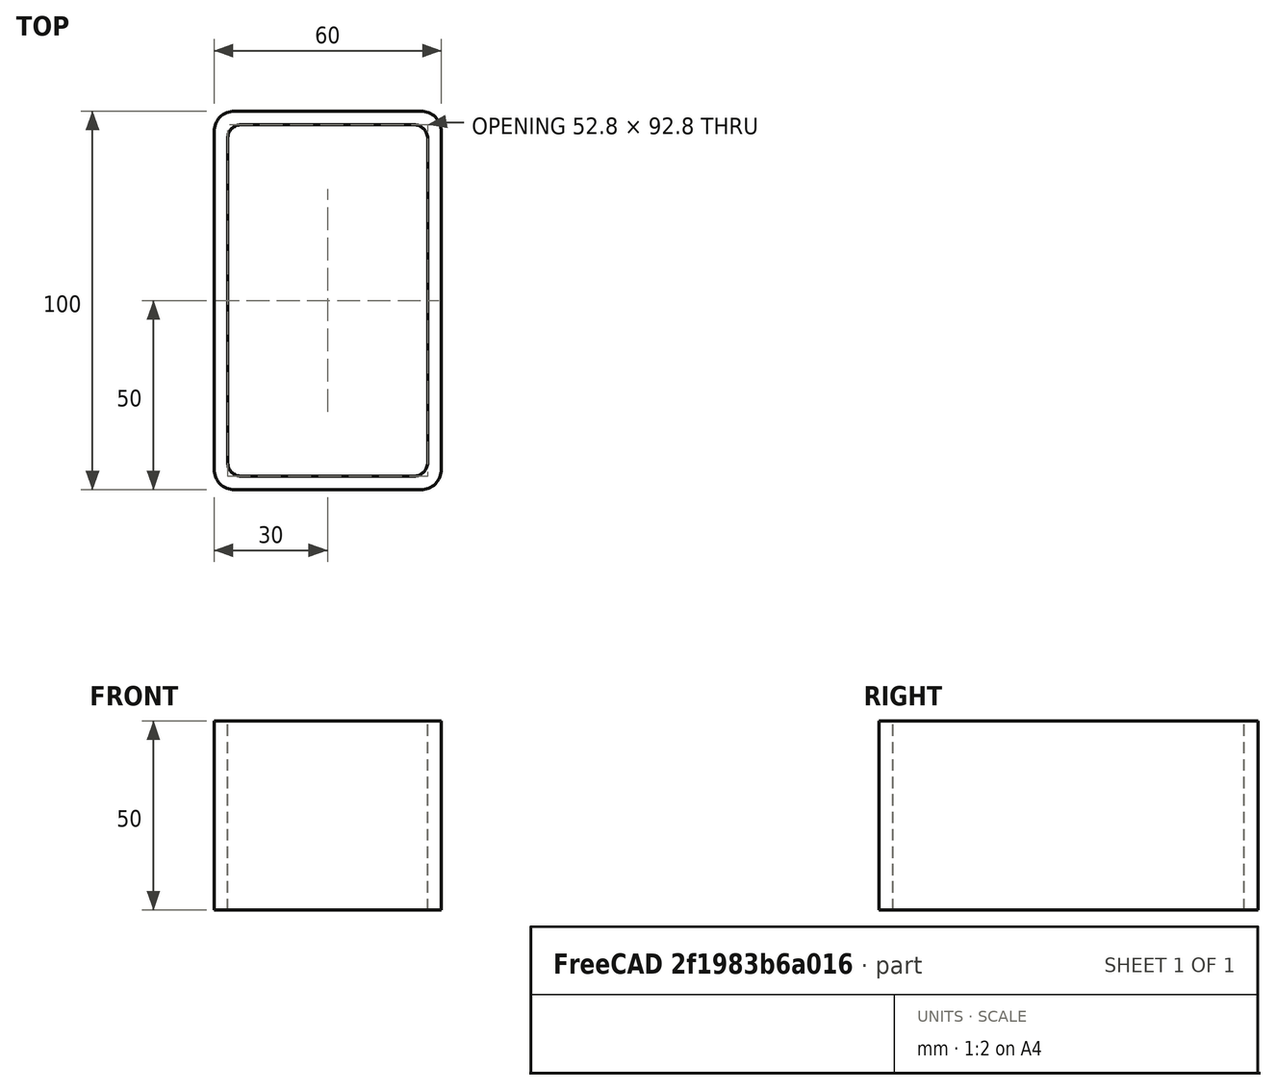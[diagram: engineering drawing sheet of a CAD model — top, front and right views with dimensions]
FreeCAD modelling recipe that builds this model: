
FCSTD DOCUMENT  (FreeCAD 0.15R4671 (Git))
Label: Rectangular hollow section 100x60x3.6 EN10219 S235JRH
License: All rights reserved
LicenseURL: http://en.wikipedia.org/wiki/All_rights_reserved
objects: Sketcher::SketchObject×1, Part::Extrusion×1
note: 2 computed .brp shape members not serialized (recipe doc carries the construction recipe); baked Part::Feature solids carry a one-line shape summary decoded from their .brp

FEATURE [Sketcher::SketchObject] Sketch
  sketch-geometry (16):
    g0: LineSegment StartX=-22.8 StartY=46.4 StartZ=0 EndX=22.8 EndY=46.4 EndZ=0
    g1: LineSegment StartX=26.4 StartY=42.8 StartZ=0 EndX=26.4 EndY=-42.8 EndZ=0
    g2: LineSegment StartX=22.8 StartY=-46.4 StartZ=0 EndX=-22.8 EndY=-46.4 EndZ=0
    g3: LineSegment StartX=-26.4 StartY=-42.8 StartZ=0 EndX=-26.4 EndY=42.8 EndZ=0
    g4: LineSegment StartX=-24.6 StartY=50 StartZ=0 EndX=24.6 EndY=50 EndZ=0
    g5: LineSegment StartX=30 StartY=44.6 StartZ=0 EndX=30 EndY=-44.6 EndZ=0
    g6: LineSegment StartX=24.6 StartY=-50 StartZ=0 EndX=-24.6 EndY=-50 EndZ=0
    g7: LineSegment StartX=-30 StartY=-44.6 StartZ=0 EndX=-30 EndY=44.6 EndZ=0
    g8: ArcOfCircle CenterX=-22.8 CenterY=42.8 CenterZ=0 NormalX=0 NormalY=0 NormalZ=1 Radius=3.6 StartAngle=1.5708 EndAngle=3.14159
    g9: ArcOfCircle CenterX=22.8 CenterY=42.8 CenterZ=0 NormalX=0 NormalY=0 NormalZ=1 Radius=3.6 StartAngle=0 EndAngle=1.5708
    g10: ArcOfCircle CenterX=22.8 CenterY=-42.8 CenterZ=0 NormalX=0 NormalY=0 NormalZ=1 Radius=3.6 StartAngle=4.71239 EndAngle=6.28319
    g11: ArcOfCircle CenterX=-22.8 CenterY=-42.8 CenterZ=0 NormalX=0 NormalY=0 NormalZ=1 Radius=3.6 StartAngle=3.14159 EndAngle=4.71239
    g12: ArcOfCircle CenterX=24.6 CenterY=44.6 CenterZ=0 NormalX=0 NormalY=0 NormalZ=1 Radius=5.4 StartAngle=0 EndAngle=1.5708
    g13: ArcOfCircle CenterX=24.6 CenterY=-44.6 CenterZ=0 NormalX=0 NormalY=0 NormalZ=1 Radius=5.4 StartAngle=4.71239 EndAngle=6.28319
    g14: ArcOfCircle CenterX=-24.6 CenterY=-44.6 CenterZ=0 NormalX=0 NormalY=0 NormalZ=1 Radius=5.4 StartAngle=3.14159 EndAngle=4.71239
    g15: ArcOfCircle CenterX=-24.6 CenterY=44.6 CenterZ=0 NormalX=0 NormalY=0 NormalZ=1 Radius=5.4 StartAngle=1.5708 EndAngle=3.14159
  constraints (36):
    c: Horizontal(g2)
    c: Vertical(g3)
    c: Horizontal(g6)
    c: Vertical(g7)
    c: Tangent(g3,g8) = 1.5708
    c: Tangent(g0,g8) = 1.5708
    c: Tangent(g0,g9) = 1.5708
    c: Tangent(g1,g9) = 1.5708
    c: Tangent(g1,g10) = 1.5708
    c: Tangent(g2,g10) = 1.5708
    c: Tangent(g2,g11) = 1.5708
    c: Tangent(g3,g11) = 1.5708
    c: Tangent(g4,g12) = 1.5708
    c: Tangent(g5,g12) = 1.5708
    c: Tangent(g5,g13) = 1.5708
    c: Tangent(g6,g13) = 1.5708
    c: Tangent(g6,g14) = 1.5708
    c: Tangent(g7,g14) = 1.5708
    c: Tangent(g7,g15) = 1.5708
    c: Tangent(g4,g15) = 1.5708
    c: Equal(g9,g8)
    c: Equal(g9,g11)
    c: Equal(g9,g10)
    c: Equal(g12,g15)
    c: Equal(g12,g14)
    c: Equal(g12,g13)
    c: Symmetric(g4,g6,g-1)
    c: Symmetric(g7,g5,g-2)
    c: DistanceY(g4,g6) = -100
    c: DistanceX(g7,g5) = 60
    c: Symmetric(g3,g1,g-2)
    c: Symmetric(g0,g2,g-1)
    c: DistanceY(g0,g4) = 3.6
    c: DistanceX(g5,g1) = -3.6
    c: Radius(g9) = 3.6
    c: Radius(g12) = 5.4
FEATURE [Part::Extrusion] Extrude  label="Rectangular hollow section 100x60x3.6 EN10219 S235JRH"
  Base = -> Sketch
  Dir = (0,0,50)
  Solid = true
